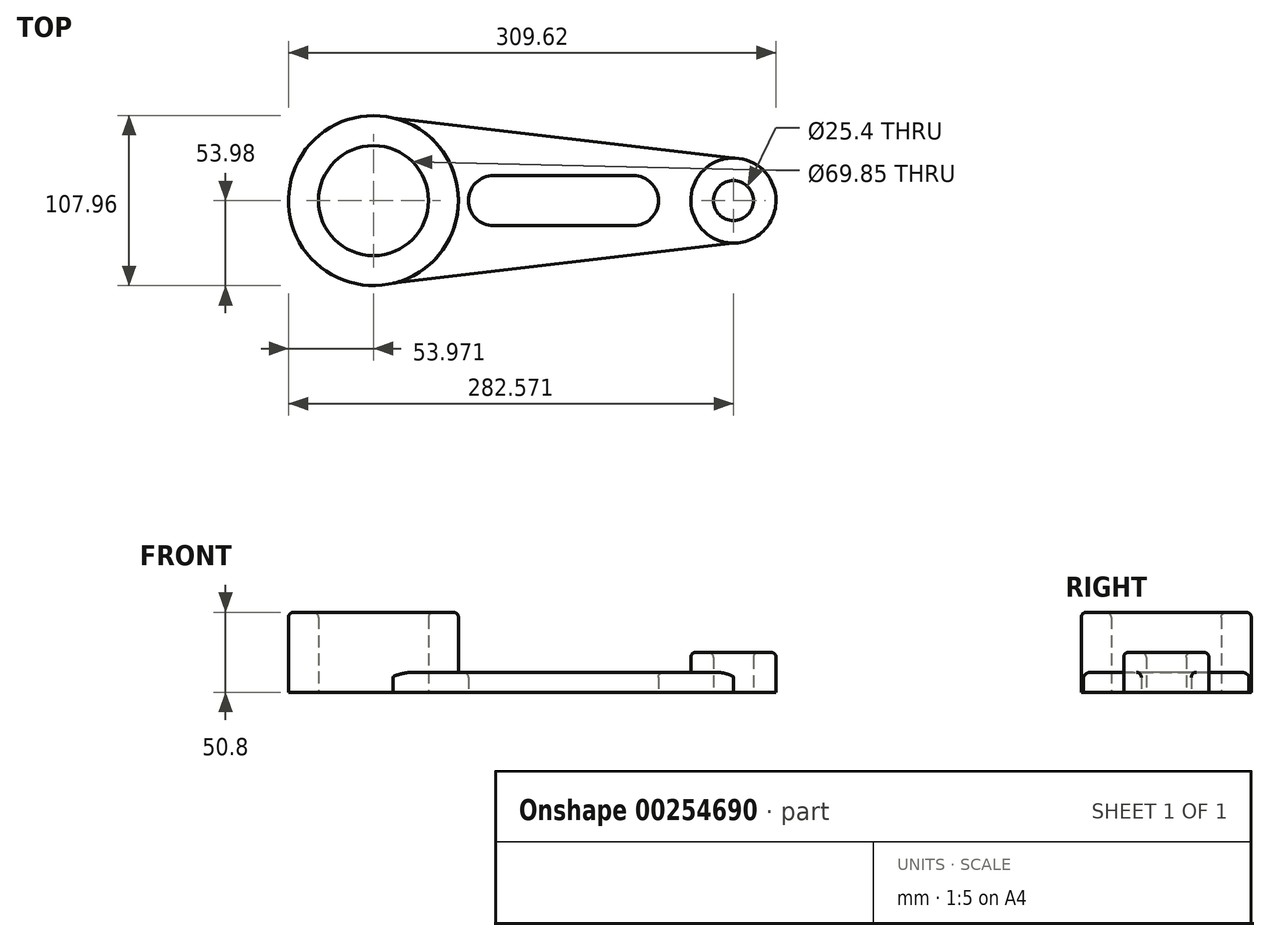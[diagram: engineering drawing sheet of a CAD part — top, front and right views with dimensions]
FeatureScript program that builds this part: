
annotation { "Feature Type Name" : "Feature", "Feature Type Description" : "" }
export const myFeature = defineFeature(function(context is Context, id is Id, definition is map)
    precondition{}
    {
        {
            var Q0;
            Q0=qCreatedBy(makeId("Top.planeOp"),FACE);
            var sketch = newSketch(context, id + "F0", { "sketchPlane" : qUnion([Q0])});
            skCircle(sketch, "E0", {"center": v(-34.26, 0) * mm, "radius": 34.93 * mm});
            skCircle(sketch, "E1", {"center": v(194.34, 0) * mm, "radius": 12.7 * mm});
            skCircle(sketch, "E2", {"center": v(-34.26, 0) * mm, "radius": 53.98 * mm});
            skCircle(sketch, "E3", {"center": v(194.34, 0) * mm, "radius": 27.05 * mm});
            skLineSegment(sketch, "E4", {"start": v(-34.26, 53.97) * mm, "end": v(194.34, 27.05) * mm});
            skLineSegment(sketch, "E5", {"start": v(-34.26, -53.97) * mm, "end": v(194.34, -27.05) * mm});
            skArc(sketch, "E6", {"start": v(41.94, 15.88) * mm, "mid": v(26.07, 0) * mm, "end": v(41.94, -15.88) * mm});
            skArc(sketch, "E7", {"start": v(130.84, -15.88) * mm, "mid": v(146.72, 0) * mm, "end": v(130.84, 15.88) * mm});
            skLineSegment(sketch, "E8", {"start": v(41.94, 15.88) * mm, "end": v(130.84, 15.88) * mm});
            skLineSegment(sketch, "E9", {"start": v(41.94, -15.88) * mm, "end": v(130.84, -15.88) * mm});
            skSolve(sketch);
        }
        {
            var Q0;
            Q0 = qSketchRegion(id + "F0", true);
            extrude(context, id + "F1", {"entities" : qUnion([Q0]), "depth" : 12.7 * mm});
        }
        {
            var Q0;
            Q0=makeQuery(id+"F1.opExtrude","CAP_FACE",FACE,{"disambiguationData":[OSD([sQuery(id+"F0.wireOp",EDGE,"E0"),sQuery(id+"F0.wireOp",EDGE,"E1"),sQuery(id+"F0.wireOp",EDGE,"E2"),sQuery(id+"F0.wireOp",EDGE,"E3"),sQuery(id+"F0.wireOp",EDGE,"E4"),sQuery(id+"F0.wireOp",EDGE,"E5"),sQuery(id+"F0.wireOp",EDGE,"E6"),sQuery(id+"F0.wireOp",EDGE,"E7"),sQuery(id+"F0.wireOp",EDGE,"E8"),sQuery(id+"F0.wireOp",EDGE,"E9")])],"isStart":false});
            var sketch = newSketch(context, id + "F2", { "sketchPlane" : qUnion([Q0])});
            skCircle(sketch, "E10", {"center": v(-34.26, 0) * mm, "radius": 34.93 * mm});
            skCircle(sketch, "E11", {"center": v(-34.26, 0) * mm, "radius": 53.98 * mm});
            skSolve(sketch);
        }
        {
            var Q0;
            Q0 = qSketchRegion(id + "F2", true);
            extrude(context, id + "F3", {"entities" : qUnion([Q0]), "operationType" : NewBodyOperationType.ADD, "depth" : 38.1 * mm});
        }
        {
            var Q0;
            Q0=makeQuery(id+"F1.opExtrude","CAP_FACE",FACE,{"disambiguationData":[OSD([sQuery(id+"F0.wireOp",EDGE,"E0"),sQuery(id+"F0.wireOp",EDGE,"E1"),sQuery(id+"F0.wireOp",EDGE,"E2"),sQuery(id+"F0.wireOp",EDGE,"E3"),sQuery(id+"F0.wireOp",EDGE,"E4"),sQuery(id+"F0.wireOp",EDGE,"E5"),sQuery(id+"F0.wireOp",EDGE,"E6"),sQuery(id+"F0.wireOp",EDGE,"E7"),sQuery(id+"F0.wireOp",EDGE,"E8"),sQuery(id+"F0.wireOp",EDGE,"E9")])],"isStart":false});
            var sketch = newSketch(context, id + "F4", { "sketchPlane" : qUnion([Q0])});
            skCircle(sketch, "E12", {"center": v(194.34, 0) * mm, "radius": 12.7 * mm});
            skCircle(sketch, "E13", {"center": v(194.34, 0) * mm, "radius": 27.05 * mm});
            skSolve(sketch);
        }
        {
            var Q0;
            Q0 = qSketchRegion(id + "F4", true);
            extrude(context, id + "F5", {"entities" : qUnion([Q0]), "operationType" : NewBodyOperationType.ADD, "depth" : 12.7 * mm});
        }
        {
            var Q0;
            Q0=makeQuery(id+"F3.opExtrude","CAP_EDGE",EDGE,{"disambiguationData":[OSD([sQuery(id+"F2.wireOp",EDGE,"E11")])],"isStart":false});
            var Q1;
            Q1=makeQuery(id+"F1.opExtrude","CAP_EDGE",EDGE,{"disambiguationData":[OSD([sQuery(id+"F0.wireOp",EDGE,"E4")])],"isStart":false});
            var Q2;
            Q2=makeQuery(id+"F1.opExtrude","CAP_EDGE",EDGE,{"disambiguationData":[OSD([sQuery(id+"F0.wireOp",EDGE,"E5")])],"isStart":false});
            var Q3;
            Q3=makeQuery(id+"F5.opExtrude","CAP_EDGE",EDGE,{"disambiguationData":[OSD([sQuery(id+"F4.wireOp",EDGE,"E13")])],"isStart":false});
            fillet(context, id + "F6", {"entities" : qUnion([Q0, Q1, Q2, Q3]), "radius" : 3.17 * mm, "tangentPropagation" : true, "allowEdgeOverflow" : false});
        }
        {
            var Q0;
            Q0=makeQuery(id+"F3.opExtrude","CAP_EDGE",EDGE,{"disambiguationData":[OSD([sQuery(id+"F2.wireOp",EDGE,"E10")])],"isStart":false});
            var Q1;
            Q1=makeQuery(id+"F1.opExtrude","CAP_EDGE",EDGE,{"disambiguationData":[OSD([sQuery(id+"F0.wireOp",EDGE,"E8")])],"isStart":false});
            var Q2;
            Q2=makeQuery(id+"F1.opExtrude","CAP_EDGE",EDGE,{"disambiguationData":[OSD([sQuery(id+"F0.wireOp",EDGE,"E6")])],"isStart":false});
            var Q3;
            Q3=makeQuery(id+"F1.opExtrude","CAP_EDGE",EDGE,{"disambiguationData":[OSD([sQuery(id+"F0.wireOp",EDGE,"E9")])],"isStart":false});
            var Q4;
            Q4=makeQuery(id+"F1.opExtrude","CAP_EDGE",EDGE,{"disambiguationData":[OSD([sQuery(id+"F0.wireOp",EDGE,"E7")])],"isStart":false});
            var Q5;
            Q5=makeQuery(id+"F5.opExtrude","CAP_EDGE",EDGE,{"disambiguationData":[OSD([sQuery(id+"F4.wireOp",EDGE,"E12")])],"isStart":false});
            fillet(context, id + "F7", {"entities" : qUnion([Q0, Q1, Q2, Q3, Q4, Q5]), "radius" : 3.17 * mm, "tangentPropagation" : true, "allowEdgeOverflow" : false});
        }
    });
